# Revit family: STELO
name_source: partatom
category: Осветительные приборы
revit_build: Autodesk Revit 2016 (Build: 20150220_1215(x64)
units: mm (PartAtom-declared; Revit-internal decimal feet)

## family parameters
Источник света = Да
Общий = Нет
Основа = Грань
При загрузке вырезать с полостями = Нет
Размер круглого соединителя = Использовать диаметр
Тип детали = Нормальный
Точка расчета площади = Нет

## types (4) — shared parameters
ADSK_Единица измерения = Шт.
ADSK_Завод-изготовитель = ООО МГК Световые технологии
ADSK_Количество фаз = 1
ADSK_Количество фаз числовое = 1
ADSK_Масса = 0.8
ADSK_Наименование = Настенный светильник, создающий диффузное освещение. Рассеиватель из выдувного трехслойного опалового стекла ручной работы. Установочная плата из окрашенного белой матовой краской металла.
ADSK_Напряжение = 230 В
ADSK_Номинальная мощность = 0 кВт
ADSK_Полная мощность = 0 кВ·А
ADSK_Размер_Высота = 300 мм
ADSK_Размер_Радиус = 72 мм
ADSK_Размер_Ширина = 150 мм
ADSK_Ток = 0 А
IP Class = IP20
URL = http://ltcompany.com
a = 10 мм
c = 150 мм
e = 120 мм
Блок аварийного питания = Нет
Видимая форма излучения при визуализации = Нет
Группа модели = Светильники
Изготовитель = ООО МГК Световые технологии
Излучение по длине прямоугольника = 150 мм
Излучение по ширине прямоугольника = 300 мм
Класс Защиты = I
Климатическая зона = УХЛ4
Код по классификатору = D5020200
Корпус = Серый металл
Область использования = Гостиницы, Индивидуальные дома, Культурно-развлекательные, Магазины/Бутики, Объекты бытового обслуживания, Объекты общественного питания, Офисы, ТРЦ
Описание = Настенный светильник, создающий диффузное освещение. Рассеиватель из выдувного трехслойного опалового стекла ручной работы. Установочная плата из окрашенного белой матовой краской металла.
Отметка по умолчанию = 120 мм
Плафон = Плафон полупрозрачный
Полная установленная мощность = 0 кВ·А
Разработчик = ООО ПРОРУБИМ
Разработчик (телефон) = +7 (495) 649-85-43
Светофильтр = 16777215
Смещение цветовой температуры при затухании лампы = <Нет>
Тип продукции = Светильник
Файл фотометрической сетки = STELO.IES

## per-type parameters (varying)
| type | ADSK_Код изделия | ADSK_Коэффициент мощности | ADSK_Энергоэффективность | Тип ИС | Тип ПРА | УГО | Угол наклона |
| Stelo LED 14 3000K | 1565000010
1548000010
1548000010 | 0.96 | 65 лм/Вт | LED | Драйвер | Да | 0.00° |
| Stelo 118 | 1549000010 | 0.5 | 67 лм/Вт | КЛЛ | ЭПРА | Нет | 0.00° |
| Stelo 160 | 1549000020 | 1 | 9 лм/Вт | ЛН | Без ПРА | Нет | 0.00° |
| Stelo LED 9 3000K | 1565000020 | 0.96 | 70 лм/Вт | LED | Драйвер | Да | 90.00° |
